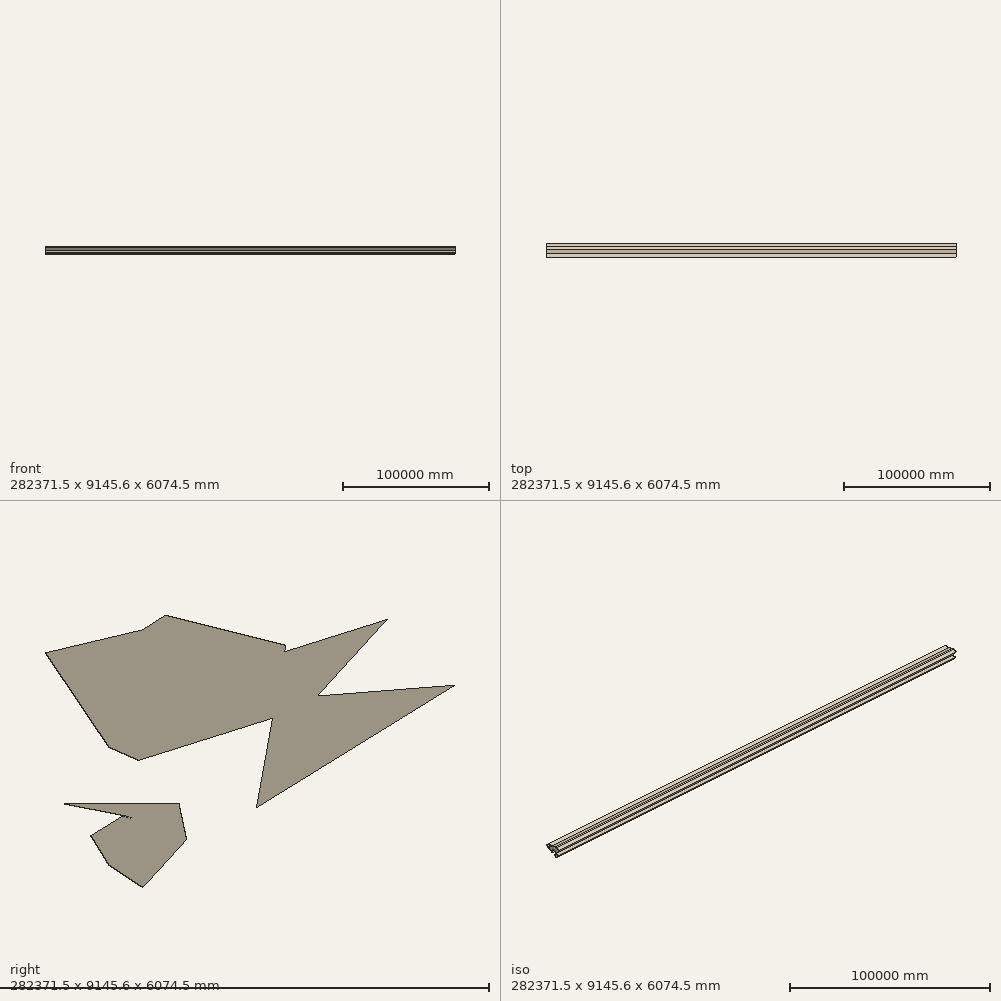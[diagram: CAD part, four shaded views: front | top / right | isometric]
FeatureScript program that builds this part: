
annotation { "Feature Type Name" : "Feature", "Feature Type Description" : "" }
export const myFeature = defineFeature(function(context is Context, id is Id, definition is map)
    precondition{}
    {
        {
            var Q0;
            Q0=qCreatedBy(makeId("Front.planeOp"),FACE);
            var sketch = newSketch(context, id + "F0", { "sketchPlane" : qUnion([Q0])});
            skCircle(sketch, "E0", {"center": v(0, 0) * mm, "radius": 15.42 * mm});
            skCircle(sketch, "E1", {"center": v(0, 0) * mm, "radius": 20.79 * mm});
            skCircle(sketch, "E2", {"center": v(0, 0) * mm, "radius": 25.99 * mm});
            skCircle(sketch, "E3", {"center": v(0, 0) * mm, "radius": 7.43 * mm});
            skCircle(sketch, "E4", {"center": v(0, 0) * mm, "radius": 31.36 * mm});
            skCircle(sketch, "E5", {"center": v(0, 0) * mm, "radius": 4.09 * mm});
            skCircle(sketch, "E6", {"center": v(0, 0) * mm, "radius": 13.35 * mm});
            skCircle(sketch, "E7", {"center": v(0, 0) * mm, "radius": 18.55 * mm});
            skCircle(sketch, "E8", {"center": v(0, 0) * mm, "radius": 23.82 * mm});
            skCircle(sketch, "E9", {"center": v(0, 0) * mm, "radius": 28.33 * mm});
            skCircle(sketch, "E10", {"center": v(0, 0) * mm, "radius": 6.33 * mm});
            skCircle(sketch, "E11", {"center": v(0, 0) * mm, "radius": 1.65 * mm});
            skCircle(sketch, "E12", {"center": v(0, 0) * mm, "radius": 9.13 * mm});
            skCircle(sketch, "E13", {"center": v(0, 0) * mm, "radius": 10.77 * mm});
            skCircle(sketch, "E14", {"center": v(0, 0) * mm, "radius": 17.1 * mm});
            skCircle(sketch, "E15", {"center": v(0, 0) * mm, "radius": 11.74 * mm});
            skCircle(sketch, "E16", {"center": v(0, 0) * mm, "radius": 22.11 * mm});
            skCircle(sketch, "E17", {"center": v(0, -1.65) * mm, "radius": 29.07 * mm});
            skCircle(sketch, "E18", {"center": v(0, -1.65) * mm, "radius": 34.86 * mm});
            skSolve(sketch);
        }
        {
            var Q0;
            Q0=makeQuery(id+"F0.imprint","IMPRINT",FACE,{"disambiguationData":[TD([[makeQuery(id+"F0.imprint","IMPRINT",EDGE,{"derivedFrom":sQuery(id+"F0.wireOp",EDGE,"E5")}),1.0]])]});
            var Q1;
            Q1=makeQuery(id+"F0.imprint","IMPRINT",FACE,{"disambiguationData":[TD([[makeQuery(id+"F0.imprint","IMPRINT",EDGE,{"derivedFrom":sQuery(id+"F0.wireOp",EDGE,"E3")}),1.0]])]});
            var Q2;
            Q2=makeQuery(id+"F0.imprint","IMPRINT",FACE,{"disambiguationData":[TD([[makeQuery(id+"F0.imprint","IMPRINT",EDGE,{"derivedFrom":sQuery(id+"F0.wireOp",EDGE,"E12")}),-1.0]])]});
            var Q3;
            Q3=makeQuery(id+"F0.imprint","IMPRINT",FACE,{"disambiguationData":[TD([[makeQuery(id+"F0.imprint","IMPRINT",EDGE,{"derivedFrom":sQuery(id+"F0.wireOp",EDGE,"E1")}),1.0]])]});
            var Q4;
            Q4=makeQuery(id+"F0.imprint","IMPRINT",FACE,{"disambiguationData":[TD([[makeQuery(id+"F0.imprint","IMPRINT",EDGE,{"derivedFrom":sQuery(id+"F0.wireOp",EDGE,"E2")}),-1.0]])]});
            var Q5;
            Q5=makeQuery(id+"F0.imprint","IMPRINT",FACE,{"disambiguationData":[TD([[makeQuery(id+"F0.imprint","IMPRINT",EDGE,{"derivedFrom":sQuery(id+"F0.wireOp",EDGE,"E4")}),1.0]])]});
            var Q6;
            Q6=makeQuery(id+"F0.imprint","IMPRINT",FACE,{"disambiguationData":[TD([[makeQuery(id+"F0.imprint","IMPRINT",EDGE,{"derivedFrom":sQuery(id+"F0.wireOp",EDGE,"E4")}),-1.0]])]});
            var Q7;
            Q7=makeQuery(id+"F0.imprint","IMPRINT",FACE,{"disambiguationData":[TD([[makeQuery(id+"F0.imprint","IMPRINT",EDGE,{"derivedFrom":sQuery(id+"F0.wireOp",EDGE,"E2")}),1.0]])]});
            var Q8;
            Q8=makeQuery(id+"F0.imprint","IMPRINT",FACE,{"disambiguationData":[TD([[makeQuery(id+"F0.imprint","IMPRINT",EDGE,{"derivedFrom":sQuery(id+"F0.wireOp",EDGE,"E8")}),1.0]])]});
            var Q9;
            Q9=makeQuery(id+"F0.imprint","IMPRINT",FACE,{"disambiguationData":[TD([[makeQuery(id+"F0.imprint","IMPRINT",EDGE,{"derivedFrom":sQuery(id+"F0.wireOp",EDGE,"E0")}),-1.0]])]});
            var Q10;
            Q10=makeQuery(id+"F0.imprint","IMPRINT",FACE,{"disambiguationData":[TD([[makeQuery(id+"F0.imprint","IMPRINT",EDGE,{"derivedFrom":sQuery(id+"F0.wireOp",EDGE,"E0")}),1.0]])]});
            var Q11;
            {var subQ0=sQuery(id+"F0.wireOp",EDGE,"E17");var subQ1=sQuery(id+"F0.wireOp",EDGE,"E9");var subQ2=makeQuery(id+"F0.imprint","INTERSECT",VERTEX,{"disambiguationData":[OD(0.0)],"derivedFrom":[subQ1,subQ0]});Q11=makeQuery(id+"F0.imprint","IMPRINT",FACE,{"disambiguationData":[TD([[makeQuery(id+"F0.imprint","IMPRINT",EDGE,{"disambiguationData":[TD([[subQ2,-1.0]])],"derivedFrom":subQ1}),-1.0]])]});}
            var Q12;
            Q12=makeQuery(id+"F0.imprint","IMPRINT",FACE,{"disambiguationData":[TD([[makeQuery(id+"F0.imprint","IMPRINT",EDGE,{"derivedFrom":sQuery(id+"F0.wireOp",EDGE,"E1")}),-1.0]])]});
            var Q13;
            Q13=makeQuery(id+"F0.imprint","IMPRINT",FACE,{"disambiguationData":[TD([[makeQuery(id+"F0.imprint","IMPRINT",EDGE,{"derivedFrom":sQuery(id+"F0.wireOp",EDGE,"E7")}),1.0]])]});
            var Q14;
            Q14=makeQuery(id+"F0.imprint","IMPRINT",FACE,{"disambiguationData":[TD([[makeQuery(id+"F0.imprint","IMPRINT",EDGE,{"derivedFrom":sQuery(id+"F0.wireOp",EDGE,"E6")}),1.0]])]});
            var Q15;
            Q15=makeQuery(id+"F0.imprint","IMPRINT",FACE,{"disambiguationData":[TD([[makeQuery(id+"F0.imprint","IMPRINT",EDGE,{"derivedFrom":sQuery(id+"F0.wireOp",EDGE,"E13")}),-1.0]])]});
            var Q16;
            Q16=makeQuery(id+"F0.imprint","IMPRINT",FACE,{"disambiguationData":[TD([[makeQuery(id+"F0.imprint","IMPRINT",EDGE,{"derivedFrom":sQuery(id+"F0.wireOp",EDGE,"E3")}),-1.0]])]});
            var Q17;
            Q17=makeQuery(id+"F0.imprint","IMPRINT",FACE,{"disambiguationData":[TD([[makeQuery(id+"F0.imprint","IMPRINT",EDGE,{"derivedFrom":sQuery(id+"F0.wireOp",EDGE,"E5")}),-1.0]])]});
            var Q18;
            {var subQ0=sQuery(id+"F0.wireOp",EDGE,"E17");var subQ1=sQuery(id+"F0.wireOp",EDGE,"E9");var subQ2=makeQuery(id+"F0.imprint","INTERSECT",VERTEX,{"disambiguationData":[OD(0.0)],"derivedFrom":[subQ1,subQ0]});Q18=makeQuery(id+"F0.imprint","IMPRINT",FACE,{"disambiguationData":[TD([[makeQuery(id+"F0.imprint","IMPRINT",EDGE,{"disambiguationData":[TD([[subQ2,1.0]])],"derivedFrom":subQ1}),1.0]])]});}
            extrude(context, id + "F1", {"entities" : qUnion([Q0, Q1, Q2, Q3, Q4, Q5, Q6, Q7, Q8, Q9, Q10, Q11, Q12, Q13, Q14, Q15, Q16, Q17, Q18]), "depth" : 355.6 * mm, "offsetDistance" : 25.4 * mm});
        }
        {
            var Q0;
            Q0=qCreatedBy(makeId("Front.planeOp"),FACE);
            var sketch = newSketch(context, id + "F2", { "sketchPlane" : qUnion([Q0])});
            skCircle(sketch, "E19", {"center": v(-13.46, 14.42) * mm, "radius": 12.8 * mm});
            skCircle(sketch, "E20", {"center": v(-4.13, 23.17) * mm, "radius": 2.73 * mm});
            skCircle(sketch, "E21", {"center": v(-4.13, 23.17) * mm, "radius": 17.53 * mm});
            skCircle(sketch, "E22", {"center": v(-4.13, 23.17) * mm, "radius": 85.15 * mm});
            skCircle(sketch, "E23", {"center": v(-11.74, 14.42) * mm, "radius": 65.63 * mm});
            skCircle(sketch, "E24", {"center": v(-13.46, 14.42) * mm, "radius": 69.3 * mm});
            skCircle(sketch, "E25", {"center": v(-11.74, 14.42) * mm, "radius": 93.99 * mm});
            skCircle(sketch, "E26", {"center": v(-4.13, 23.17) * mm, "radius": 119.04 * mm});
            skCircle(sketch, "E27", {"center": v(-4.13, 23.17) * mm, "radius": 147.94 * mm});
            skSolve(sketch);
        }
        {
            var Q0;
            Q0=makeQuery(id+"F2.imprint","IMPRINT",FACE,{"disambiguationData":[TD([[makeQuery(id+"F2.imprint","IMPRINT",EDGE,{"derivedFrom":sQuery(id+"F2.wireOp",EDGE,"E26")}),-1.0]])]});
            var Q1;
            {var subQ0=sQuery(id+"F2.wireOp",EDGE,"E25");var subQ1=sQuery(id+"F2.wireOp",EDGE,"E22");var subQ2=makeQuery(id+"F2.imprint","INTERSECT",VERTEX,{"disambiguationData":[OD(0.0)],"derivedFrom":[subQ1,subQ0]});Q1=makeQuery(id+"F2.imprint","IMPRINT",FACE,{"disambiguationData":[TD([[makeQuery(id+"F2.imprint","IMPRINT",EDGE,{"disambiguationData":[TD([[subQ2,-1.0]])],"derivedFrom":subQ1}),-1.0]])]});}
            var Q2;
            Q2=makeQuery(id+"F2.imprint","IMPRINT",FACE,{"disambiguationData":[TD([[makeQuery(id+"F2.imprint","IMPRINT",EDGE,{"derivedFrom":sQuery(id+"F2.wireOp",EDGE,"E26")}),1.0]])]});
            var Q3;
            Q3=makeQuery(id+"F2.imprint","IMPRINT",FACE,{"disambiguationData":[TD([[makeQuery(id+"F2.imprint","IMPRINT",EDGE,{"derivedFrom":sQuery(id+"F2.wireOp",EDGE,"E23")}),1.0]])]});
            var Q4;
            Q4=makeQuery(id+"F2.imprint","IMPRINT",FACE,{"disambiguationData":[TD([[makeQuery(id+"F2.imprint","IMPRINT",EDGE,{"derivedFrom":sQuery(id+"F2.wireOp",EDGE,"E24")}),-1.0]])]});
            extrude(context, id + "F3", {"entities" : qUnion([Q0, Q1, Q2, Q3, Q4]), "operationType" : NewBodyOperationType.ADD, "depth" : 533.4 * mm, "offsetDistance" : 25.4 * mm, "hasSecondDirection" : true, "secondDirectionOppositeDirection" : true, "secondDirectionDepth" : 25.4 * mm});
        }
        {
            var Q0;
            Q0=makeQuery(id+"F3.opExtrude","CAP_FACE",FACE,{"disambiguationData":[OSD([sQuery(id+"F2.wireOp",EDGE,"E19"),sQuery(id+"F2.wireOp",EDGE,"E21"),sQuery(id+"F2.wireOp",EDGE,"E23")])],"isStart":false});
            var Q1;
            Q1=makeQuery(id+"F3.opExtrude","CAP_FACE",FACE,{"disambiguationData":[OSD([sQuery(id+"F2.wireOp",EDGE,"E22"),sQuery(id+"F2.wireOp",EDGE,"E24"),sQuery(id+"F2.wireOp",EDGE,"E25"),sQuery(id+"F2.wireOp",EDGE,"E27")])],"isStart":false});
            extrude(context, id + "F4", {"entities" : qUnion([Q0, Q1]), "depth" : 25.4 * mm, "offsetDistance" : 25.4 * mm});
        }
        {
            var Q0;
            Q0=qCreatedBy(makeId("Right.planeOp"),FACE);
            var sketch = newSketch(context, id + "F5", { "sketchPlane" : qUnion([Q0])});
            skLineSegment(sketch, "E28", {"start": v(-2711.51, -900.17) * mm, "end": v(-1082.71, 839.92) * mm});
            skLineSegment(sketch, "E29", {"start": v(-1082.71, 839.92) * mm, "end": v(1598.24, 172.21) * mm});
            skLineSegment(sketch, "E30", {"start": v(1598.24, 172.21) * mm, "end": v(1598.24, -1365.54) * mm});
            skLineSegment(sketch, "E31", {"start": v(-2711.51, -900.17) * mm, "end": v(1598.24, -1365.54) * mm});
            skLineSegment(sketch, "E32", {"start": v(-2711.51, -900.17) * mm, "end": v(-1679.6, -2397.45) * mm});
            skLineSegment(sketch, "E33", {"start": v(-1679.6, -2397.45) * mm, "end": v(1598.24, -1365.54) * mm});
            skLineSegment(sketch, "E34", {"start": v(-1588.55, 516.18) * mm, "end": v(-3763.66, 0) * mm});
            skLineSegment(sketch, "E35", {"start": v(-3763.66, 0) * mm, "end": v(-2347.3, -2104.07) * mm});
            skLineSegment(sketch, "E36", {"start": v(-2347.3, -2104.07) * mm, "end": v(-2711.51, -900.17) * mm});
            skLineSegment(sketch, "E37", {"start": v(-1588.55, 516.18) * mm, "end": v(-2711.51, -900.17) * mm});
            skLineSegment(sketch, "E38", {"start": v(-2347.3, -2104.07) * mm, "end": v(-1679.6, -2397.45) * mm});
            skLineSegment(sketch, "E39", {"start": v(-1588.55, 516.18) * mm, "end": v(-1082.71, 839.92) * mm});
            skLineSegment(sketch, "E40", {"start": v(1598.24, 172.21) * mm, "end": v(940.65, -3459.72) * mm});
            skLineSegment(sketch, "E41", {"start": v(940.65, -3459.72) * mm, "end": v(5381.92, -718.07) * mm});
            skLineSegment(sketch, "E42", {"start": v(5381.92, -718.07) * mm, "end": v(-2844.45, -1365.54) * mm});
            skLineSegment(sketch, "E43", {"start": v(-2844.45, -1365.54) * mm, "end": v(3865.08, 746.72) * mm});
            skLineSegment(sketch, "E44", {"start": v(3865.08, 746.72) * mm, "end": v(-1376.1, -5007.59) * mm});
            skLineSegment(sketch, "E45", {"start": v(-1376.1, -5007.59) * mm, "end": v(-1588.55, -5234.56) * mm});
            skLineSegment(sketch, "E46", {"start": v(-1588.55, -5234.56) * mm, "end": v(-2347.3, -4734.43) * mm});
            skLineSegment(sketch, "E47", {"start": v(-2347.3, -4734.43) * mm, "end": v(-2750.78, -4080.85) * mm});
            skLineSegment(sketch, "E48", {"start": v(-2750.78, -4080.85) * mm, "end": v(-2035.95, -3639.58) * mm});
            skLineSegment(sketch, "E49", {"start": v(-1517.73, -3520.42) * mm, "end": v(-1335.63, -3459.72) * mm});
            skLineSegment(sketch, "E50", {"start": v(-789.32, -3348.43) * mm, "end": v(-3450.04, -3348.43) * mm});
            skLineSegment(sketch, "E51", {"start": v(-3450.04, -3348.43) * mm, "end": v(-1952.75, -3639.58) * mm});
            skLineSegment(sketch, "E52", {"start": v(-1952.75, -3639.58) * mm, "end": v(-1517.73, -3520.42) * mm});
            skLineSegment(sketch, "E53", {"start": v(-1952.75, -3639.58) * mm, "end": v(-613.13, -4169.92) * mm});
            skLineSegment(sketch, "E54", {"start": v(-613.13, -4169.92) * mm, "end": v(-789.32, -3348.43) * mm});
            skLineSegment(sketch, "E55", {"start": v(-1335.63, -3459.72) * mm, "end": v(-789.32, -3348.43) * mm});
            skLineSegment(sketch, "E56", {"start": v(-2035.95, -3639.58) * mm, "end": v(-1820.98, -3691.75) * mm});
            skSolve(sketch);
        }
        {
            var Q0;
            {var subQ1=sQuery(id+"F5.wireOp",EDGE,"E45");Q0=makeQuery(id+"F5.imprint","IMPRINT",FACE,{"disambiguationData":[TD([[makeQuery(id+"F5.imprint","IMPRINT",EDGE,{"derivedFrom":subQ1}),-1.0]])]});}
            var Q1;
            Q1=makeQuery(id+"F5.imprint","IMPRINT",FACE,{"disambiguationData":[TD([[makeQuery(id+"F5.imprint","IMPRINT",EDGE,{"derivedFrom":sQuery(id+"F5.wireOp",EDGE,"E49")}),-1.0]])]});
            var Q2;
            Q2=makeQuery(id+"F5.imprint","IMPRINT",FACE,{"disambiguationData":[TD([[makeQuery(id+"F5.imprint","IMPRINT",EDGE,{"derivedFrom":sQuery(id+"F5.wireOp",EDGE,"E49")}),1.0]])]});
            var Q3;
            {var subQ0=sQuery(id+"F5.wireOp",EDGE,"E41");Q3=makeQuery(id+"F5.imprint","IMPRINT",FACE,{"disambiguationData":[TD([[makeQuery(id+"F5.imprint","IMPRINT",EDGE,{"derivedFrom":subQ0}),1.0]])]});}
            var Q4;
            {var subQ0=sQuery(id+"F5.wireOp",EDGE,"E44");var subQ5=sQuery(id+"F5.wireOp",EDGE,"E40");var subQ6=makeQuery(id+"F5.imprint","INTERSECT",VERTEX,{"derivedFrom":[subQ5,subQ0]});Q4=makeQuery(id+"F5.imprint","IMPRINT",FACE,{"disambiguationData":[TD([[makeQuery(id+"F5.imprint","IMPRINT",EDGE,{"disambiguationData":[TD([[subQ6,1.0]])],"derivedFrom":subQ5}),1.0]])]});}
            var Q5;
            {var subQ0=sQuery(id+"F5.wireOp",EDGE,"E43");var subQ1=sQuery(id+"F5.wireOp",EDGE,"E30");var subQ2=makeQuery(id+"F5.imprint","INTERSECT",VERTEX,{"derivedFrom":[subQ1,subQ0]});Q5=makeQuery(id+"F5.imprint","IMPRINT",FACE,{"disambiguationData":[TD([[makeQuery(id+"F5.imprint","IMPRINT",EDGE,{"disambiguationData":[TD([[subQ2,-1.0]])],"derivedFrom":subQ1}),1.0]])]});}
            var Q6;
            {var subQ0=sQuery(id+"F5.wireOp",EDGE,"E43");var subQ1=sQuery(id+"F5.wireOp",EDGE,"E31");var subQ2=makeQuery(id+"F5.imprint","INTERSECT",VERTEX,{"derivedFrom":[subQ1,subQ0]});Q6=makeQuery(id+"F5.imprint","IMPRINT",FACE,{"disambiguationData":[TD([[makeQuery(id+"F5.imprint","IMPRINT",EDGE,{"disambiguationData":[TD([[subQ2,-1.0]])],"derivedFrom":subQ1}),1.0]])]});}
            var Q7;
            {var subQ0=sQuery(id+"F5.wireOp",EDGE,"E43");var subQ1=sQuery(id+"F5.wireOp",EDGE,"E31");var subQ2=makeQuery(id+"F5.imprint","INTERSECT",VERTEX,{"derivedFrom":[subQ1,subQ0]});Q7=makeQuery(id+"F5.imprint","IMPRINT",FACE,{"disambiguationData":[TD([[makeQuery(id+"F5.imprint","IMPRINT",EDGE,{"disambiguationData":[TD([[subQ2,-1.0]])],"derivedFrom":subQ1}),-1.0]])]});}
            var Q8;
            {var subQ1=sQuery(id+"F5.wireOp",EDGE,"E31");var subQ3=sQuery(id+"F5.wireOp",EDGE,"E43");var subQ4=makeQuery(id+"F5.imprint","INTERSECT",VERTEX,{"derivedFrom":[subQ1,subQ3]});Q8=makeQuery(id+"F5.imprint","IMPRINT",FACE,{"disambiguationData":[TD([[makeQuery(id+"F5.imprint","IMPRINT",EDGE,{"disambiguationData":[TD([[subQ4,1.0]])],"derivedFrom":subQ3}),1.0]])]});}
            var Q9;
            {var subQ0=sQuery(id+"F5.wireOp",EDGE,"E38");Q9=makeQuery(id+"F5.imprint","IMPRINT",FACE,{"disambiguationData":[TD([[makeQuery(id+"F5.imprint","IMPRINT",EDGE,{"derivedFrom":subQ0}),1.0]])]});}
            var Q10;
            {var subQ0=sQuery(id+"F5.wireOp",EDGE,"E36");var subQ3=sQuery(id+"F5.wireOp",EDGE,"E42");var subQ5=makeQuery(id+"F5.imprint","INTERSECT",VERTEX,{"derivedFrom":[subQ0,subQ3]});Q10=makeQuery(id+"F5.imprint","IMPRINT",FACE,{"disambiguationData":[TD([[makeQuery(id+"F5.imprint","IMPRINT",EDGE,{"disambiguationData":[TD([[subQ5,1.0]])],"derivedFrom":subQ0}),1.0]])]});}
            var Q11;
            {var subQ2=sQuery(id+"F5.wireOp",EDGE,"E34");Q11=makeQuery(id+"F5.imprint","IMPRINT",FACE,{"disambiguationData":[TD([[makeQuery(id+"F5.imprint","IMPRINT",EDGE,{"derivedFrom":subQ2}),1.0]])]});}
            var Q12;
            {var subQ5=sQuery(id+"F5.wireOp",EDGE,"E28");Q12=makeQuery(id+"F5.imprint","IMPRINT",FACE,{"disambiguationData":[TD([[makeQuery(id+"F5.imprint","IMPRINT",EDGE,{"derivedFrom":subQ5}),-1.0]])]});}
            var Q13;
            Q13=makeQuery(id+"F5.imprint","IMPRINT",FACE,{"disambiguationData":[TD([[makeQuery(id+"F5.imprint","IMPRINT",EDGE,{"derivedFrom":sQuery(id+"F5.wireOp",EDGE,"E28")}),1.0]])]});
            var Q14;
            {var subQ1=sQuery(id+"F5.wireOp",EDGE,"E32");var subQ3=sQuery(id+"F5.wireOp",EDGE,"E43");var subQ4=makeQuery(id+"F5.imprint","INTERSECT",VERTEX,{"derivedFrom":[subQ1,subQ3]});Q14=makeQuery(id+"F5.imprint","IMPRINT",FACE,{"disambiguationData":[TD([[makeQuery(id+"F5.imprint","IMPRINT",EDGE,{"disambiguationData":[TD([[subQ4,1.0]])],"derivedFrom":subQ3}),1.0]])]});}
            var Q15;
            {var subQ0=sQuery(id+"F5.wireOp",EDGE,"E43");var subQ1=sQuery(id+"F5.wireOp",EDGE,"E32");var subQ2=makeQuery(id+"F5.imprint","INTERSECT",VERTEX,{"derivedFrom":[subQ1,subQ0]});Q15=makeQuery(id+"F5.imprint","IMPRINT",FACE,{"disambiguationData":[TD([[makeQuery(id+"F5.imprint","IMPRINT",EDGE,{"disambiguationData":[TD([[subQ2,-1.0]])],"derivedFrom":subQ1}),-1.0]])]});}
            var Q16;
            {var subQ0=sQuery(id+"F5.wireOp",EDGE,"E42");var subQ1=sQuery(id+"F5.wireOp",EDGE,"E36");var subQ2=makeQuery(id+"F5.imprint","INTERSECT",VERTEX,{"derivedFrom":[subQ1,subQ0]});Q16=makeQuery(id+"F5.imprint","IMPRINT",FACE,{"disambiguationData":[TD([[makeQuery(id+"F5.imprint","IMPRINT",EDGE,{"disambiguationData":[TD([[subQ2,-1.0]])],"derivedFrom":subQ1}),1.0]])]});}
            var Q17;
            {var subQ0=sQuery(id+"F5.wireOp",EDGE,"E42");var subQ1=sQuery(id+"F5.wireOp",EDGE,"E31");var subQ2=makeQuery(id+"F5.imprint","INTERSECT",VERTEX,{"derivedFrom":[subQ1,subQ0]});Q17=makeQuery(id+"F5.imprint","IMPRINT",FACE,{"disambiguationData":[TD([[makeQuery(id+"F5.imprint","IMPRINT",EDGE,{"disambiguationData":[TD([[subQ2,-1.0]])],"derivedFrom":subQ1}),1.0]])]});}
            var Q18;
            {var subQ0=sQuery(id+"F5.wireOp",EDGE,"E31");var subQ5=sQuery(id+"F5.wireOp",EDGE,"E40");var subQ6=makeQuery(id+"F5.imprint","INTERSECT",VERTEX,{"derivedFrom":[subQ0,subQ5]});Q18=makeQuery(id+"F5.imprint","IMPRINT",FACE,{"disambiguationData":[TD([[makeQuery(id+"F5.imprint","IMPRINT",EDGE,{"disambiguationData":[TD([[subQ6,1.0]])],"derivedFrom":subQ5}),1.0]])]});}
            var Q19;
            {var subQ0=sQuery(id+"F5.wireOp",EDGE,"E43");var subQ1=sQuery(id+"F5.wireOp",EDGE,"E30");var subQ2=makeQuery(id+"F5.imprint","INTERSECT",VERTEX,{"derivedFrom":[subQ1,subQ0]});Q19=makeQuery(id+"F5.imprint","IMPRINT",FACE,{"disambiguationData":[TD([[makeQuery(id+"F5.imprint","IMPRINT",EDGE,{"disambiguationData":[TD([[subQ2,-1.0]])],"derivedFrom":subQ1}),-1.0]])]});}
            var Q20;
            {var subQ0=sQuery(id+"F5.wireOp",EDGE,"E33");var subQ3=sQuery(id+"F5.wireOp",EDGE,"E40");var subQ5=makeQuery(id+"F5.imprint","INTERSECT",VERTEX,{"derivedFrom":[subQ0,subQ3]});Q20=makeQuery(id+"F5.imprint","IMPRINT",FACE,{"disambiguationData":[TD([[makeQuery(id+"F5.imprint","IMPRINT",EDGE,{"disambiguationData":[TD([[subQ5,1.0]])],"derivedFrom":subQ3}),1.0]])]});}
            var Q21;
            {var subQ3=sQuery(id+"F5.wireOp",EDGE,"E31");var subQ7=sQuery(id+"F5.wireOp",EDGE,"E42");var subQ9=makeQuery(id+"F5.imprint","INTERSECT",VERTEX,{"derivedFrom":[subQ3,subQ7]});Q21=makeQuery(id+"F5.imprint","IMPRINT",FACE,{"disambiguationData":[TD([[makeQuery(id+"F5.imprint","IMPRINT",EDGE,{"disambiguationData":[TD([[subQ9,-1.0]])],"derivedFrom":subQ3}),-1.0]])]});}
            extrude(context, id + "F6", {"entities" : qUnion([Q0, Q1, Q2, Q3, Q4, Q5, Q6, Q7, Q8, Q9, Q10, Q11, Q12, Q13, Q14, Q15, Q16, Q17, Q18, Q19, Q20, Q21]), "depth" : 282219.4 * mm, "offsetDistance" : 25.4 * mm});
        }
    });
